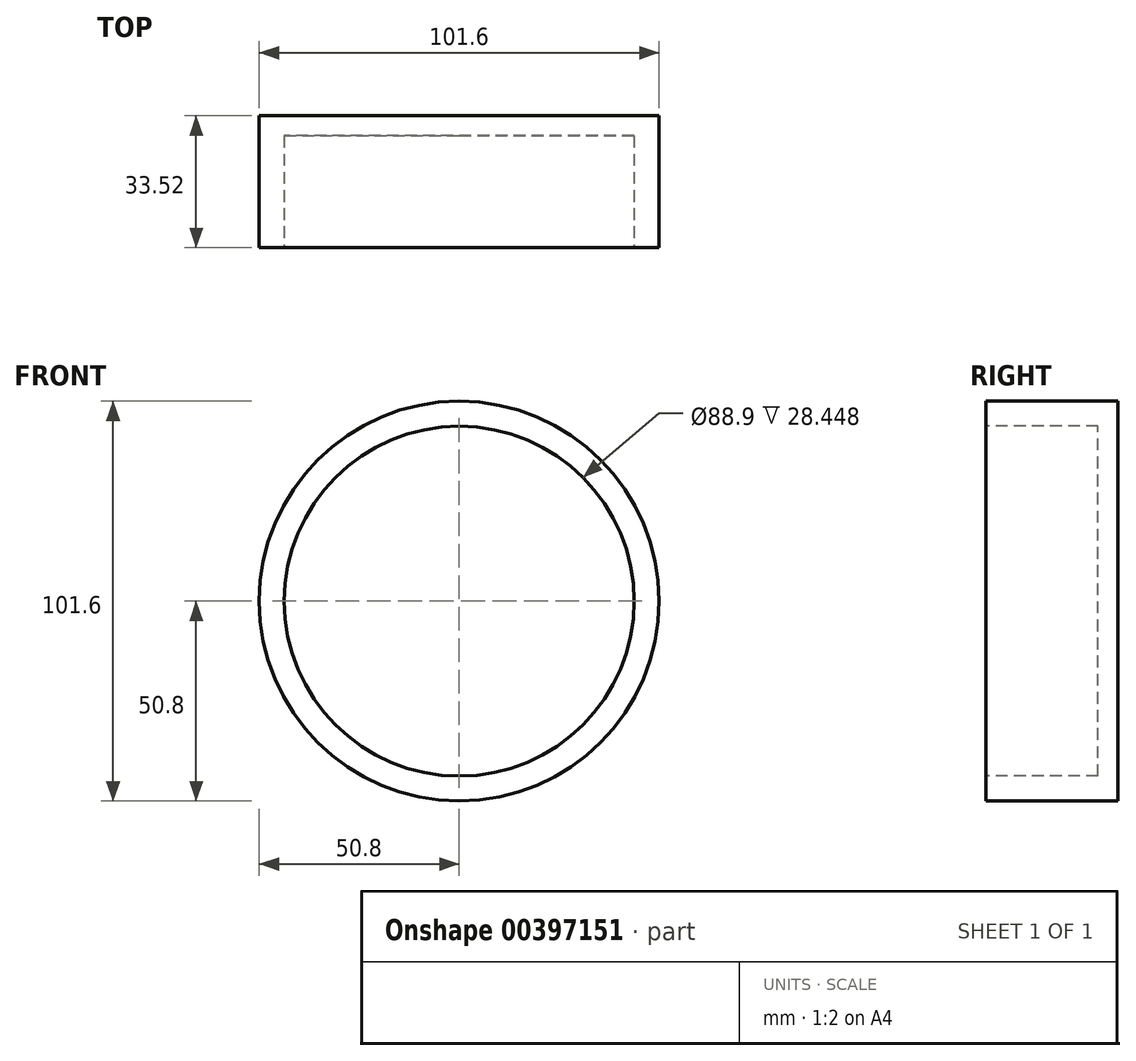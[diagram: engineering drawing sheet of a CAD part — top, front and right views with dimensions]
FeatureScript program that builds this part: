
annotation { "Feature Type Name" : "Feature", "Feature Type Description" : "" }
export const myFeature = defineFeature(function(context is Context, id is Id, definition is map)
    precondition{}
    {
        {
            var Q0;
            Q0=qCreatedBy(makeId("Front.planeOp"),FACE);
            var sketch = newSketch(context, id + "F0", { "sketchPlane" : qUnion([Q0])});
            skCircle(sketch, "E0", {"center": v(0, 0) * mm, "radius": 50.8 * mm});
            skSolve(sketch);
        }
        {
            var Q0;
            Q0=makeQuery(id+"F0.imprint","IMPRINT",FACE,{"disambiguationData":[TD([[makeQuery(id+"F0.imprint","IMPRINT",EDGE,{"derivedFrom":sQuery(id+"F0.wireOp",EDGE,"E0")}),1.0]])]});
            extrude(context, id + "F1", {"entities" : qUnion([Q0]), "depth" : 16.76 * mm, "hasSecondDirection" : true, "secondDirectionOppositeDirection" : true, "secondDirectionDepth" : 16.76 * mm});
        }
        {
            var Q0;
            Q0=makeQuery(id+"F1.opExtrude","CAP_FACE",FACE,{"disambiguationData":[OSD([sQuery(id+"F0.wireOp",EDGE,"E0")])],"isStart":false});
            var sketch = newSketch(context, id + "F2", { "sketchPlane" : qUnion([Q0])});
            skCircle(sketch, "E1", {"center": v(0, 0) * mm, "radius": 44.45 * mm});
            skSolve(sketch);
        }
        {
            var Q0;
            Q0=makeQuery(id+"F2.imprint","IMPRINT",FACE,{"disambiguationData":[TD([[makeQuery(id+"F2.imprint","IMPRINT",EDGE,{"derivedFrom":sQuery(id+"F2.wireOp",EDGE,"E1")}),1.0]])]});
            extrude(context, id + "F3", {"entities" : qUnion([Q0]), "operationType" : NewBodyOperationType.REMOVE, "oppositeDirection" : true, "depth" : 28.45 * mm});
        }
    });
